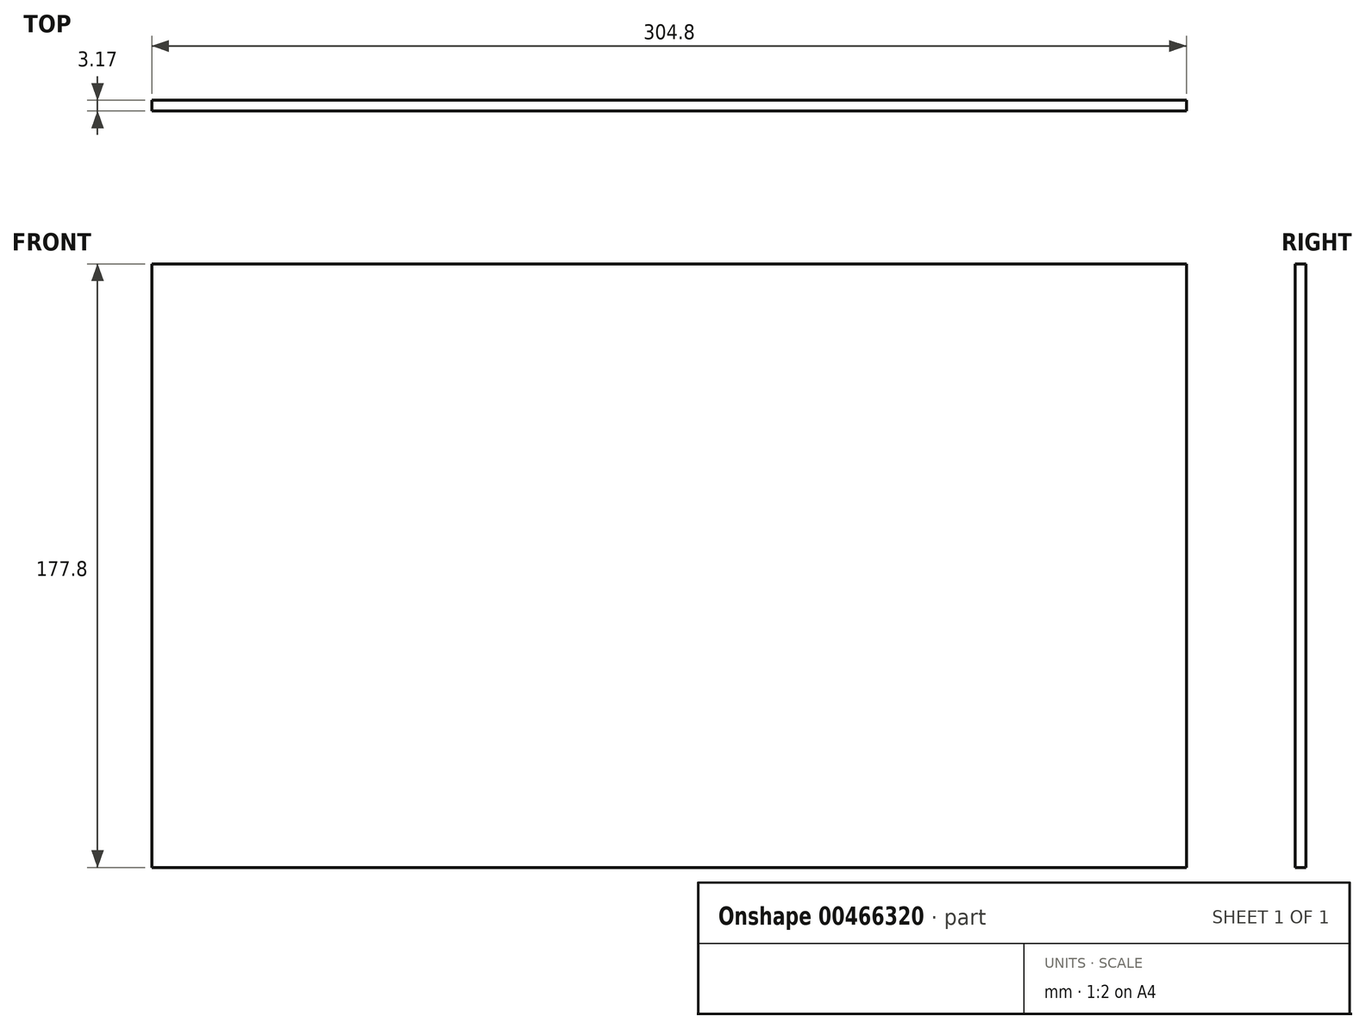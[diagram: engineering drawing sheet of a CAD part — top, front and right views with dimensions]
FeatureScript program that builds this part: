
annotation { "Feature Type Name" : "Feature", "Feature Type Description" : "" }
export const myFeature = defineFeature(function(context is Context, id is Id, definition is map)
    precondition{}
    {
        {
            var Q0;
            Q0=qCreatedBy(makeId("Front.planeOp"),FACE);
            var sketch = newSketch(context, id + "F0", { "sketchPlane" : qUnion([Q0])});
            skLineSegment(sketch, "E0.bottom", {"start": v(-59.58, 157.08) * mm, "end": v(245.22, 157.08) * mm});
            skLineSegment(sketch, "E0.top", {"start": v(-59.58, -20.72) * mm, "end": v(245.22, -20.72) * mm});
            skLineSegment(sketch, "E0.left", {"start": v(-59.58, 157.08) * mm, "end": v(-59.58, -20.72) * mm});
            skLineSegment(sketch, "E0.right", {"start": v(245.22, 157.08) * mm, "end": v(245.22, -20.72) * mm});
            skSolve(sketch);
        }
        {
            var Q0;
            Q0=makeQuery(id+"F0.imprint","IMPRINT",FACE,{"disambiguationData":[TD([[makeQuery(id+"F0.imprint","IMPRINT",EDGE,{"derivedFrom":sQuery(id+"F0.wireOp",EDGE,"E0.bottom")}),-1.0]])]});
            extrude(context, id + "F1", {"entities" : qUnion([Q0]), "depth" : 3.17 * mm});
        }
    });
